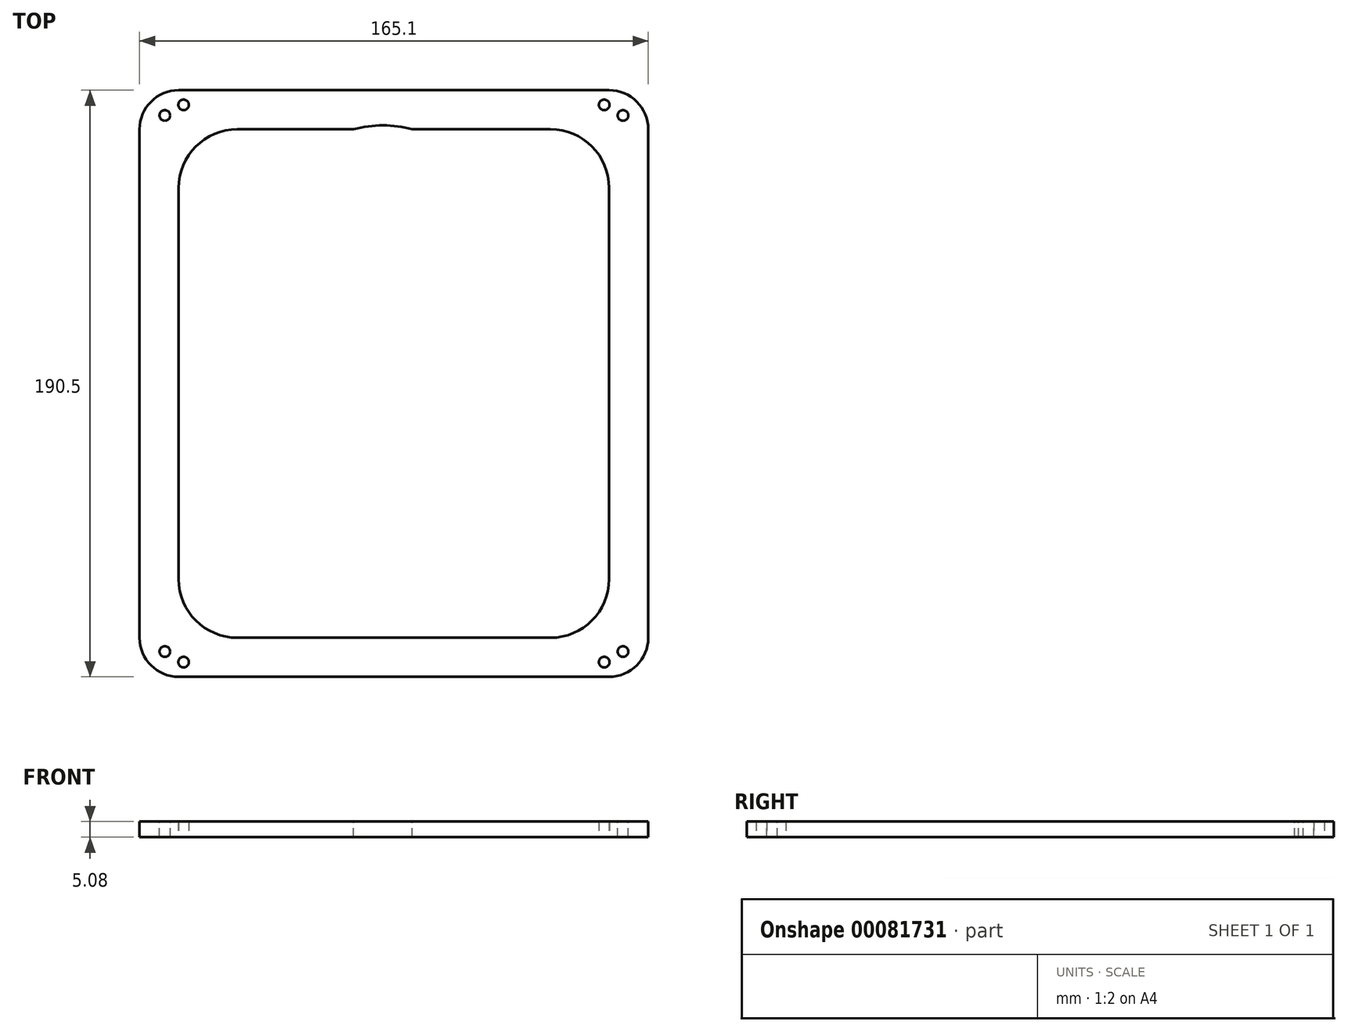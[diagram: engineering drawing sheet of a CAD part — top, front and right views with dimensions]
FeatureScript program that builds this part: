
annotation { "Feature Type Name" : "Feature", "Feature Type Description" : "" }
export const myFeature = defineFeature(function(context is Context, id is Id, definition is map)
    precondition{}
    {
        {
            var Q0;
            Q0=qCreatedBy(makeId("Top.planeOp"),FACE);
            var sketch = newSketch(context, id + "F0", { "sketchPlane" : qUnion([Q0])});
            skLineSegment(sketch, "E0.bottom", {"start": v(12.7, 0) * mm, "end": v(152.4, 0) * mm});
            skLineSegment(sketch, "E0.top", {"start": v(12.7, 190.5) * mm, "end": v(152.4, 190.5) * mm});
            skLineSegment(sketch, "E0.left", {"start": v(0, 12.7) * mm, "end": v(0, 177.8) * mm});
            skLineSegment(sketch, "E0.right", {"start": v(165.1, 12.7) * mm, "end": v(165.1, 177.8) * mm});
            skPoint(sketch, "E1.visualSharp", {"position": v(0, 190.5) * mm});
            skArc(sketch, "E1.filletArc", {"start": v(12.7, 190.5) * mm, "mid": v(3.72, 186.78) * mm, "end": v(0, 177.8) * mm});
            skPoint(sketch, "E2.visualSharp", {"position": v(165.1, 190.5) * mm});
            skArc(sketch, "E2.filletArc", {"start": v(165.1, 177.8) * mm, "mid": v(161.38, 186.78) * mm, "end": v(152.4, 190.5) * mm});
            skPoint(sketch, "E3.visualSharp", {"position": v(165.1, 0) * mm});
            skArc(sketch, "E3.filletArc", {"start": v(152.4, 0) * mm, "mid": v(161.38, 3.72) * mm, "end": v(165.1, 12.7) * mm});
            skPoint(sketch, "E4.visualSharp", {"position": v(0, 0) * mm});
            skArc(sketch, "E4.filletArc", {"start": v(0, 12.7) * mm, "mid": v(3.72, 3.72) * mm, "end": v(12.7, 0) * mm});
            skLineSegment(sketch, "E5.4", {"start": v(12.7, 177.8) * mm, "end": v(12.7, 177.8) * mm});
            skLineSegment(sketch, "E6.bottom", {"start": v(31.75, 177.8) * mm, "end": v(133.35, 177.8) * mm});
            skLineSegment(sketch, "E6.top", {"start": v(31.75, 12.7) * mm, "end": v(133.35, 12.7) * mm});
            skLineSegment(sketch, "E6.left", {"start": v(12.7, 158.75) * mm, "end": v(12.7, 31.75) * mm});
            skLineSegment(sketch, "E6.right", {"start": v(152.4, 158.75) * mm, "end": v(152.4, 31.75) * mm});
            skArc(sketch, "E7.filletArc", {"start": v(31.75, 177.8) * mm, "mid": v(18.28, 172.22) * mm, "end": v(12.7, 158.75) * mm});
            skArc(sketch, "E8.filletArc", {"start": v(152.4, 158.75) * mm, "mid": v(146.82, 172.22) * mm, "end": v(133.35, 177.8) * mm});
            skArc(sketch, "E9.filletArc", {"start": v(133.35, 12.7) * mm, "mid": v(146.82, 18.28) * mm, "end": v(152.4, 31.75) * mm});
            skArc(sketch, "E10.filletArc", {"start": v(12.7, 31.75) * mm, "mid": v(18.28, 18.28) * mm, "end": v(31.75, 12.7) * mm});
            skSolve(sketch);
        }
        {
            var Q0;
            Q0=qSketchRegion(id+"F0",true);
            extrude(context, id + "F1", {"entities" : qUnion([Q0]), "depth" : 5.08 * mm});
        }
        {
            var Q0;
            Q0=makeQuery(id+"F1.opExtrude","CAP_FACE",FACE,{"disambiguationData":[OSD([sQuery(id+"F0.wireOp",EDGE,"E0.bottom"),sQuery(id+"F0.wireOp",EDGE,"E0.top"),sQuery(id+"F0.wireOp",EDGE,"E0.left"),sQuery(id+"F0.wireOp",EDGE,"E0.right"),sQuery(id+"F0.wireOp",EDGE,"E1.filletArc"),sQuery(id+"F0.wireOp",EDGE,"E2.filletArc"),sQuery(id+"F0.wireOp",EDGE,"E3.filletArc"),sQuery(id+"F0.wireOp",EDGE,"E4.filletArc"),sQuery(id+"F0.wireOp",EDGE,"E6.bottom"),sQuery(id+"F0.wireOp",EDGE,"E6.top"),sQuery(id+"F0.wireOp",EDGE,"E6.left"),sQuery(id+"F0.wireOp",EDGE,"E6.right"),sQuery(id+"F0.wireOp",EDGE,"E7.filletArc"),sQuery(id+"F0.wireOp",EDGE,"E8.filletArc"),sQuery(id+"F0.wireOp",EDGE,"E9.filletArc"),sQuery(id+"F0.wireOp",EDGE,"E10.filletArc")])],"isStart":true});
            var sketch = newSketch(context, id + "F2", { "sketchPlane" : qUnion([Q0])});
            skLineSegment(sketch, "E11", {"start": v(0, -142.21) * mm, "end": v(0, -190.5) * mm, "construction": true});
            skLineSegment(sketch, "E12", {"start": v(0, -190.5) * mm, "end": v(29.51, -160.99) * mm, "construction": true});
            skLineSegment(sketch, "E13", {"start": v(165.1, -140.35) * mm, "end": v(165.1, -190.5) * mm, "construction": true});
            skLineSegment(sketch, "E14", {"start": v(165.1, -190.5) * mm, "end": v(133.35, -158.75) * mm, "construction": true});
            skLineSegment(sketch, "E15", {"start": v(165.1, -41.87) * mm, "end": v(165.1, 0) * mm, "construction": true});
            skLineSegment(sketch, "E16", {"start": v(165.1, 0) * mm, "end": v(133.83, -31.27) * mm, "construction": true});
            skLineSegment(sketch, "E17", {"start": v(0, -42.8) * mm, "end": v(0, 0) * mm, "construction": true});
            skLineSegment(sketch, "E18", {"start": v(0, 0) * mm, "end": v(32.9, -32.9) * mm, "construction": true});
            skPoint(sketch, "E19", {"position": v(8.2, -182.3) * mm});
            skPoint(sketch, "E20", {"position": v(156.9, -182.3) * mm});
            skPoint(sketch, "E21", {"position": v(156.9, -8.2) * mm});
            skPoint(sketch, "E22", {"position": v(8.2, -8.2) * mm});
            skSolve(sketch);
        }
        {
            var Q0;
            Q0=sQuery(id+"F2.wireOp",VERTEX,"E19");
            var Q1;
            Q1=sQuery(id+"F2.wireOp",VERTEX,"E20");
            var Q2;
            Q2=sQuery(id+"F2.wireOp",VERTEX,"E21");
            var Q3;
            Q3=sQuery(id+"F2.wireOp",VERTEX,"E22");
            var Q4;
            Q4=makeQuery(id+"F1.opExtrude","SWEPT_BODY",BODY,{"disambiguationData":[OSD([sQuery(id+"F0.wireOp",EDGE,"E0.bottom"),sQuery(id+"F0.wireOp",EDGE,"E0.top"),sQuery(id+"F0.wireOp",EDGE,"E0.left"),sQuery(id+"F0.wireOp",EDGE,"E0.right"),sQuery(id+"F0.wireOp",EDGE,"E1.filletArc"),sQuery(id+"F0.wireOp",EDGE,"E2.filletArc"),sQuery(id+"F0.wireOp",EDGE,"E3.filletArc"),sQuery(id+"F0.wireOp",EDGE,"E4.filletArc"),sQuery(id+"F0.wireOp",EDGE,"E6.bottom"),sQuery(id+"F0.wireOp",EDGE,"E6.top"),sQuery(id+"F0.wireOp",EDGE,"E6.left"),sQuery(id+"F0.wireOp",EDGE,"E6.right"),sQuery(id+"F0.wireOp",EDGE,"E7.filletArc"),sQuery(id+"F0.wireOp",EDGE,"E8.filletArc"),sQuery(id+"F0.wireOp",EDGE,"E9.filletArc"),sQuery(id+"F0.wireOp",EDGE,"E10.filletArc")])]});
            hole(context, id + "F3", {"style" : HoleStyle.SIMPLE, "endStyle" : HoleEndStyle.THROUGH, "standardTappedOrClearance" : lookupTablePath({ "standard" : "ANSI", "engagement" : "75%", "pitch" : "32 tpi", "size" : "#8", "type" : "Tapped" }), "standardBlindInLast" : lookupTablePath({ "standard" : "ANSI", "engagement" : "75%", "pitch" : "32 tpi", "size" : "#8", "type" : "Tapped" }), "holeDiameter" : 3.45 * mm, "locations" : qUnion([Q0, Q1, Q2, Q3]), "scope" : qUnion([Q4]), "isTappedThrough" : true, "majorDiameter" : 4.17 * mm, "showTappedDepth" : true, "startStyle" : HoleStartStyle.PART});
        }
        {
            var Q0;
            {var subQ0=sQuery(id+"F0.wireOp",EDGE,"E4.filletArc");var subQ1=sQuery(id+"F0.wireOp",EDGE,"E3.filletArc");var subQ2=sQuery(id+"F0.wireOp",EDGE,"E2.filletArc");var subQ3=sQuery(id+"F0.wireOp",EDGE,"E1.filletArc");var subQ4=sQuery(id+"F0.wireOp",EDGE,"E0.bottom");var subQ5=sQuery(id+"F0.wireOp",EDGE,"E0.top");var subQ6=sQuery(id+"F0.wireOp",EDGE,"E0.left");var subQ7=sQuery(id+"F0.wireOp",EDGE,"E0.right");Q0=makeQuery(id+"Fmw6Xz0gUK7uzHi_1.boolean.opBoolean","SPLIT",FACE,{"disambiguationData":[TD([makeQuery(id+"F1.opExtrude","SWEPT_FACE",FACE,{"disambiguationData":[OSD([subQ4])]})])],"derivedFrom":makeQuery(id+"F1.opExtrude","CAP_FACE",FACE,{"disambiguationData":[OSD([subQ4,subQ5,subQ6,subQ7,subQ3,subQ2,subQ1,subQ0,sQuery(id+"F0.wireOp",EDGE,"E6.bottom"),sQuery(id+"F0.wireOp",EDGE,"E6.top"),sQuery(id+"F0.wireOp",EDGE,"E6.left"),sQuery(id+"F0.wireOp",EDGE,"E6.right"),sQuery(id+"F0.wireOp",EDGE,"E7.filletArc"),sQuery(id+"F0.wireOp",EDGE,"E8.filletArc"),sQuery(id+"F0.wireOp",EDGE,"E9.filletArc"),sQuery(id+"F0.wireOp",EDGE,"E10.filletArc")])],"isStart":false})});}
            var sketch = newSketch(context, id + "F4", { "sketchPlane" : qUnion([Q0])});
            skPoint(sketch, "E23", {"position": v(14.3, 4.78) * mm});
            skPoint(sketch, "E24", {"position": v(150.8, 4.78) * mm});
            skPoint(sketch, "E25", {"position": v(14.3, 185.72) * mm});
            skPoint(sketch, "E26", {"position": v(150.8, 185.72) * mm});
            skSolve(sketch);
        }
        {
            var Q0;
            Q0=sQuery(id+"F4.wireOp",VERTEX,"E25");
            var Q1;
            Q1=sQuery(id+"F4.wireOp",VERTEX,"E26");
            var Q2;
            Q2=sQuery(id+"F4.wireOp",VERTEX,"E23");
            var Q3;
            Q3=sQuery(id+"F4.wireOp",VERTEX,"E24");
            var Q4;
            Q4=makeQuery(id+"F1.opExtrude","SWEPT_BODY",BODY,{"disambiguationData":[OSD([sQuery(id+"F0.wireOp",EDGE,"E0.bottom"),sQuery(id+"F0.wireOp",EDGE,"E0.top"),sQuery(id+"F0.wireOp",EDGE,"E0.left"),sQuery(id+"F0.wireOp",EDGE,"E0.right"),sQuery(id+"F0.wireOp",EDGE,"E1.filletArc"),sQuery(id+"F0.wireOp",EDGE,"E2.filletArc"),sQuery(id+"F0.wireOp",EDGE,"E3.filletArc"),sQuery(id+"F0.wireOp",EDGE,"E4.filletArc"),sQuery(id+"F0.wireOp",EDGE,"E6.bottom"),sQuery(id+"F0.wireOp",EDGE,"E6.top"),sQuery(id+"F0.wireOp",EDGE,"E6.left"),sQuery(id+"F0.wireOp",EDGE,"E6.right"),sQuery(id+"F0.wireOp",EDGE,"E7.filletArc"),sQuery(id+"F0.wireOp",EDGE,"E8.filletArc"),sQuery(id+"F0.wireOp",EDGE,"E9.filletArc"),sQuery(id+"F0.wireOp",EDGE,"E10.filletArc")])]});
            hole(context, id + "F5", {"style" : HoleStyle.SIMPLE, "endStyle" : HoleEndStyle.THROUGH, "holeDiameter" : 3.43 * mm, "locations" : qUnion([Q0, Q1, Q2, Q3]), "scope" : qUnion([Q4]), "isTappedThrough" : true, "startStyle" : HoleStartStyle.PART});
        }
        {
            var Q0;
            {var subQ0=sQuery(id+"F0.wireOp",EDGE,"E10.filletArc");var subQ1=sQuery(id+"F0.wireOp",EDGE,"E6.bottom");var subQ2=sQuery(id+"F0.wireOp",EDGE,"E9.filletArc");var subQ3=sQuery(id+"F0.wireOp",EDGE,"E8.filletArc");var subQ4=sQuery(id+"F0.wireOp",EDGE,"E7.filletArc");var subQ5=sQuery(id+"F0.wireOp",EDGE,"E6.top");var subQ6=sQuery(id+"F0.wireOp",EDGE,"E6.left");var subQ7=sQuery(id+"F0.wireOp",EDGE,"E6.right");Q0=makeQuery(id+"Fmw6Xz0gUK7uzHi_1.boolean.opBoolean","SPLIT",FACE,{"disambiguationData":[TD([makeQuery(id+"F1.opExtrude","SWEPT_FACE",FACE,{"disambiguationData":[OSD([subQ1])]})])],"derivedFrom":makeQuery(id+"F1.opExtrude","CAP_FACE",FACE,{"disambiguationData":[OSD([sQuery(id+"F0.wireOp",EDGE,"E0.bottom"),sQuery(id+"F0.wireOp",EDGE,"E0.top"),sQuery(id+"F0.wireOp",EDGE,"E0.left"),sQuery(id+"F0.wireOp",EDGE,"E0.right"),sQuery(id+"F0.wireOp",EDGE,"E1.filletArc"),sQuery(id+"F0.wireOp",EDGE,"E2.filletArc"),sQuery(id+"F0.wireOp",EDGE,"E3.filletArc"),sQuery(id+"F0.wireOp",EDGE,"E4.filletArc"),subQ1,subQ5,subQ6,subQ7,subQ4,subQ3,subQ2,subQ0])],"isStart":false})});}
            var sketch = newSketch(context, id + "F6", { "sketchPlane" : qUnion([Q0])});
            skCircle(sketch, "E27", {"center": v(79, 142.88) * mm, "radius": 36.2 * mm});
            skSolve(sketch);
        }
        {
            var Q0;
            Q0=qSketchRegion(id+"F6",true);
            extrude(context, id + "F7", {"entities" : qUnion([Q0]), "operationType" : NewBodyOperationType.REMOVE, "endBound" : BoundingType.THROUGH_ALL, "oppositeDirection" : true, "depth" : 25.4 * mm});
        }
    });
